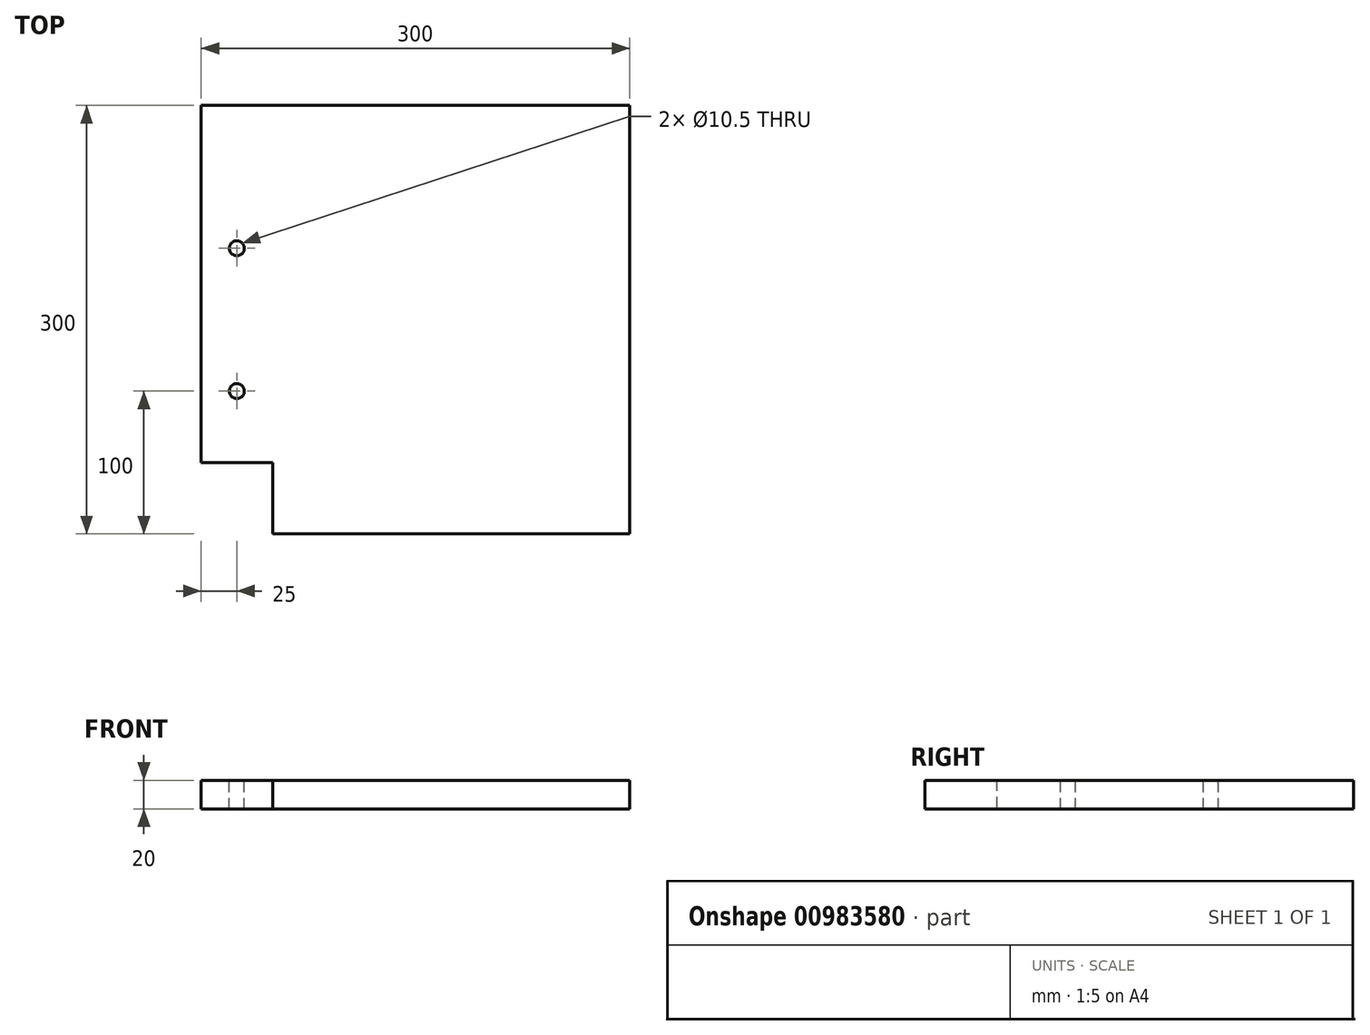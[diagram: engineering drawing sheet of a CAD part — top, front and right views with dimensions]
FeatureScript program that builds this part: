
annotation { "Feature Type Name" : "Feature", "Feature Type Description" : "" }
export const myFeature = defineFeature(function(context is Context, id is Id, definition is map)
    precondition{}
    {
        {
            var Q0;
            Q0=qCreatedBy(makeId("Top.planeOp"),FACE);
            var sketch = newSketch(context, id + "F0", { "sketchPlane" : qUnion([Q0])});
            skLineSegment(sketch, "E0", {"start": v(-150, 150) * mm, "end": v(-150, -100) * mm});
            skLineSegment(sketch, "E1", {"start": v(-150, -100) * mm, "end": v(-100, -100) * mm});
            skLineSegment(sketch, "E2", {"start": v(-100, -100) * mm, "end": v(-100, -150) * mm});
            skLineSegment(sketch, "E3", {"start": v(-100, -150) * mm, "end": v(150, -150) * mm});
            skLineSegment(sketch, "E4", {"start": v(150, -150) * mm, "end": v(150, 150) * mm});
            skLineSegment(sketch, "E5", {"start": v(150, 150) * mm, "end": v(-150, 150) * mm});
            skLineSegment(sketch, "E6", {"start": v(-125, -100) * mm, "end": v(-125, 150) * mm, "construction": true});
            skPoint(sketch, "E7", {"position": v(-125, -50) * mm});
            skPoint(sketch, "E8", {"position": v(-125, 50) * mm});
            skSolve(sketch);
        }
        {
            var Q0;
            Q0=makeQuery(id+"F0.imprint","IMPRINT",FACE,{"disambiguationData":[TD([[makeQuery(id+"F0.imprint","IMPRINT",EDGE,{"derivedFrom":sQuery(id+"F0.wireOp",EDGE,"E0")}),1.0]])]});
            extrude(context, id + "F1", {"entities" : qUnion([Q0]), "depth" : 20 * mm, "offsetDistance" : 25 * mm});
        }
        {
            var Q0;
            Q0=sQuery(id+"F0.wireOp",VERTEX,"E8");
            var Q1;
            Q1=sQuery(id+"F0.wireOp",VERTEX,"E7");
            var Q2;
            Q2=makeQuery(id+"F1.opExtrude","SWEPT_BODY",BODY,{"disambiguationData":[OSD([sQuery(id+"F0.wireOp",EDGE,"E0"),sQuery(id+"F0.wireOp",EDGE,"E1"),sQuery(id+"F0.wireOp",EDGE,"E2"),sQuery(id+"F0.wireOp",EDGE,"E3"),sQuery(id+"F0.wireOp",EDGE,"E4"),sQuery(id+"F0.wireOp",EDGE,"E5")])]});
            hole(context, id + "F2", {"style" : HoleStyle.SIMPLE, "endStyle" : HoleEndStyle.BLIND, "oppositeDirection" : true, "standardTappedOrClearance" : lookupTablePath({ "standard" : "ISO", "size" : "10.5", "type" : "Drilled" }), "standardBlindInLast" : lookupTablePath({ "standard" : "ISO", "size" : "10.5", "type" : "Drilled" }), "holeDiameter" : 10.5 * mm, "majorDiameter" : 5 * mm, "holeDepth" : 20 * mm, "isTappedThrough" : true, "tappedDepth" : 19 * mm, "tapClearance" : 3, "startFromSketch" : true, "locations" : qUnion([Q0, Q1]), "scope" : qUnion([Q2])});
        }
    });
